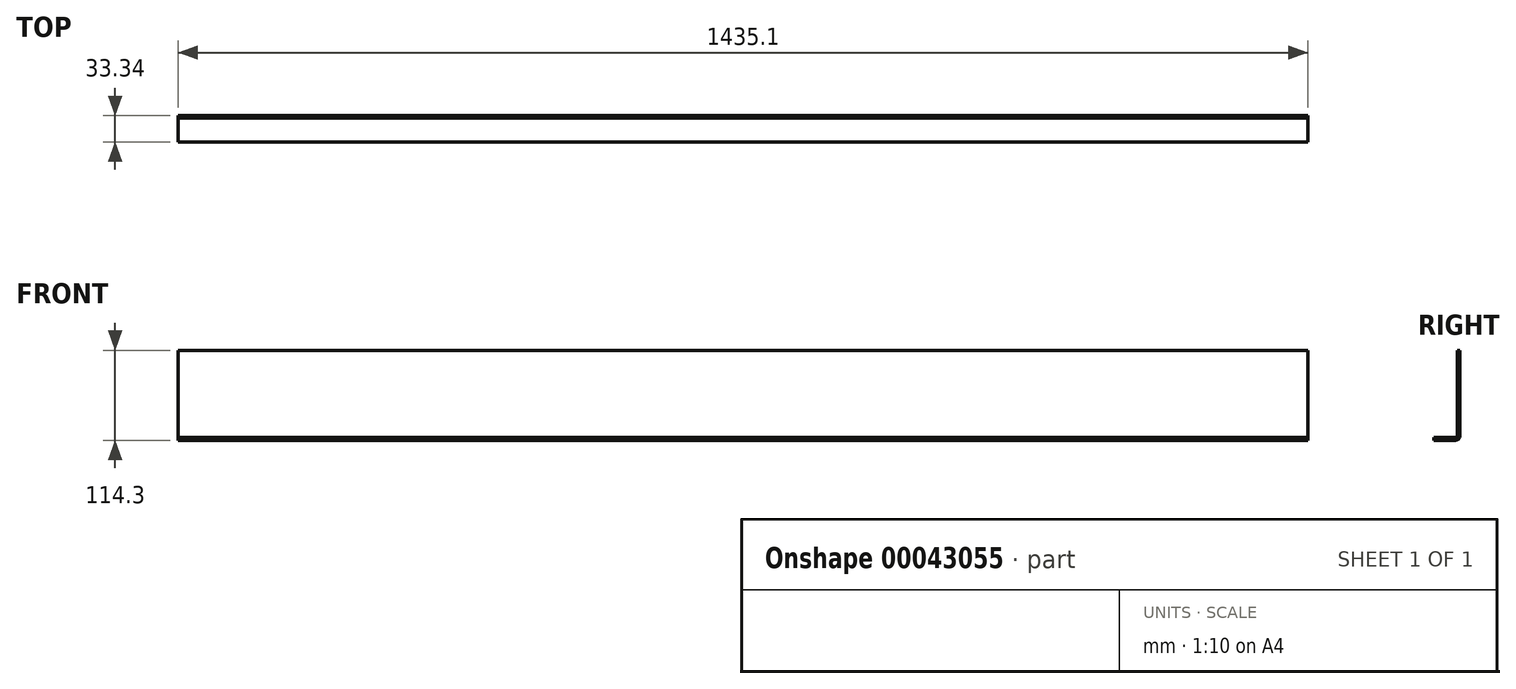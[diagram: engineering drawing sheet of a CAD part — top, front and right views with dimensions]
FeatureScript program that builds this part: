
annotation { "Feature Type Name" : "Feature", "Feature Type Description" : "" }
export const myFeature = defineFeature(function(context is Context, id is Id, definition is map)
    precondition{}
    {
        {
            var Q0;
            Q0=qCreatedBy(makeId("Right.planeOp"),FACE);
            var sketch = newSketch(context, id + "F0", { "sketchPlane" : qUnion([Q0])});
            skLineSegment(sketch, "E0", {"start": v(-33.34, -53.73) * mm, "end": v(-6.6, -53.73) * mm});
            skLineSegment(sketch, "E1", {"start": v(-3.42, 57.15) * mm, "end": v(-3.42, -50.56) * mm});
            skLineSegment(sketch, "E2", {"start": v(-3.42, 57.15) * mm, "end": v(0, 57.15) * mm});
            skLineSegment(sketch, "E3", {"start": v(0, -50.8) * mm, "end": v(0, 57.15) * mm});
            skLineSegment(sketch, "E4", {"start": v(-6.35, -57.15) * mm, "end": v(-33.34, -57.15) * mm});
            skLineSegment(sketch, "E5", {"start": v(-33.34, -53.73) * mm, "end": v(-33.34, -57.15) * mm});
            skPoint(sketch, "E6.visualSharp", {"position": v(-3.42, -53.73) * mm});
            skArc(sketch, "E6.filletArc", {"start": v(-6.6, -53.73) * mm, "mid": v(-4.35, -52.8) * mm, "end": v(-3.42, -50.56) * mm});
            skPoint(sketch, "E7.visualSharp", {"position": v(0, -57.15) * mm});
            skArc(sketch, "E7.filletArc", {"start": v(-6.35, -57.15) * mm, "mid": v(-1.86, -55.3) * mm, "end": v(0, -50.8) * mm});
            skSolve(sketch);
        }
        {
            var Q0;
            Q0=qSketchRegion(id+"F0",true);
            extrude(context, id + "F1", {"entities" : qUnion([Q0]), "endBound" : BoundingType.SYMMETRIC, "depth" : 1435.1 * mm});
        }
    });
